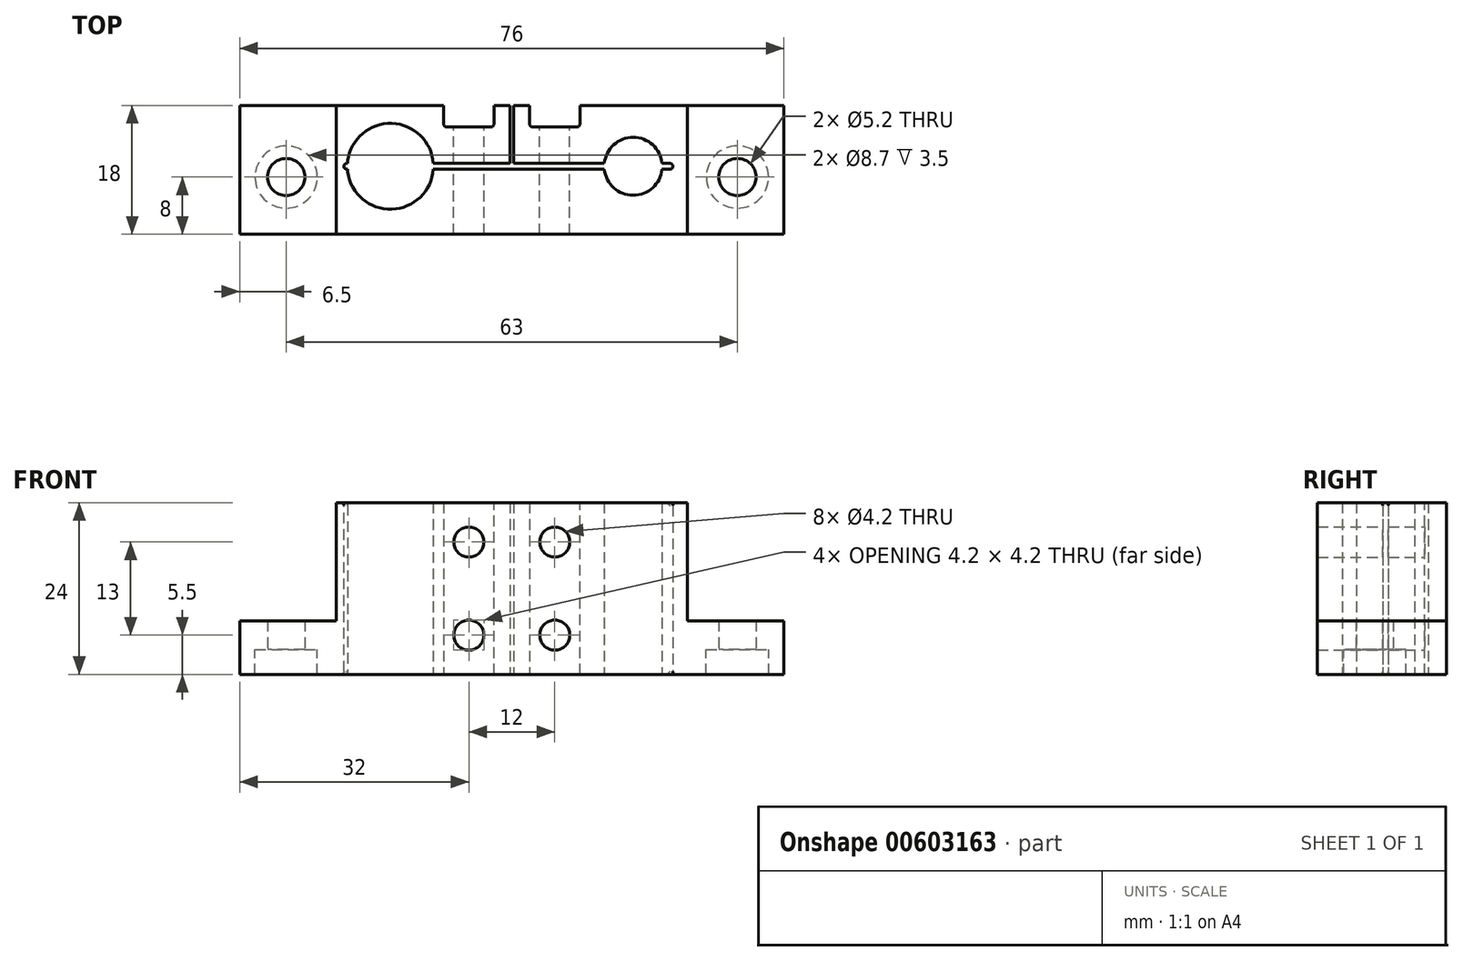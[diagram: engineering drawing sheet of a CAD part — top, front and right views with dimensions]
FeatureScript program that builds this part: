
annotation { "Feature Type Name" : "Feature", "Feature Type Description" : "" }
export const myFeature = defineFeature(function(context is Context, id is Id, definition is map)
    precondition{}
    {
        {
            var Q0;
            Q0=qCreatedBy(makeId("Top.planeOp"),FACE);
            var sketch = newSketch(context, id + "F0", { "sketchPlane" : qUnion([Q0])});
            skLineSegment(sketch, "E0.bottom", {"start": v(-38, 18) * mm, "end": v(38, 18) * mm});
            skLineSegment(sketch, "E0.top", {"start": v(-38, 0) * mm, "end": v(38, 0) * mm});
            skLineSegment(sketch, "E0.left", {"start": v(-38, 18) * mm, "end": v(-38, 0) * mm});
            skLineSegment(sketch, "E0.right", {"start": v(38, 18) * mm, "end": v(38, 0) * mm});
            skLineSegment(sketch, "E1", {"start": v(0, 0) * mm, "end": v(0, 32.17) * mm, "construction": true});
            skCircle(sketch, "E2", {"center": v(-16.95, 9.5) * mm, "radius": 6 * mm});
            skCircle(sketch, "E3", {"center": v(16.95, 9.5) * mm, "radius": 4.05 * mm});
            skCircle(sketch, "E4", {"center": v(31.5, 8) * mm, "radius": 2.6 * mm});
            skCircle(sketch, "E5", {"center": v(-31.5, 8) * mm, "radius": 2.6 * mm});
            skLineSegment(sketch, "E6", {"start": v(-24.5, 18) * mm, "end": v(-24.5, 0) * mm});
            skLineSegment(sketch, "E7", {"start": v(24.5, 18) * mm, "end": v(24.5, 0) * mm});
            skLineSegment(sketch, "E8", {"start": v(12.92, 9.1) * mm, "end": v(-10.96, 9.1) * mm});
            skLineSegment(sketch, "E9", {"start": v(12.92, 9.9) * mm, "end": v(-10.96, 9.9) * mm});
            skLineSegment(sketch, "E10", {"start": v(0.25, 9.9) * mm, "end": v(0.25, 18) * mm});
            skLineSegment(sketch, "E11", {"start": v(-0.25, 9.9) * mm, "end": v(-0.25, 18) * mm});
            skLineSegment(sketch, "E12", {"start": v(-9.5, 0) * mm, "end": v(-9.5, 3) * mm, "construction": true});
            skLineSegment(sketch, "E13", {"start": v(-9.5, 3) * mm, "end": v(-2.5, 3) * mm, "construction": true});
            skLineSegment(sketch, "E14", {"start": v(-2.5, 3) * mm, "end": v(-2.5, 0) * mm, "construction": true});
            skLineSegment(sketch, "E15.MirrorCS", {"start": v(2.5, 3) * mm, "end": v(2.5, 0) * mm, "construction": true});
            skLineSegment(sketch, "E16.MirrorCS", {"start": v(9.5, 3) * mm, "end": v(2.5, 3) * mm, "construction": true});
            skLineSegment(sketch, "E17.MirrorCS", {"start": v(9.5, 0) * mm, "end": v(9.5, 3) * mm, "construction": true});
            skLineSegment(sketch, "E18", {"start": v(-10.96, 9.9) * mm, "end": v(-22.94, 9.9) * mm, "construction": true});
            skLineSegment(sketch, "E19", {"start": v(-22.94, 9.9) * mm, "end": v(-23.45, 9.9) * mm});
            skLineSegment(sketch, "E20", {"start": v(-23.45, 9.9) * mm, "end": v(-23.45, 9.1) * mm});
            skLineSegment(sketch, "E21", {"start": v(-10.96, 9.1) * mm, "end": v(-22.94, 9.1) * mm, "construction": true});
            skLineSegment(sketch, "E22", {"start": v(-22.94, 9.1) * mm, "end": v(-23.45, 9.1) * mm});
            skLineSegment(sketch, "E23.MirrorCS", {"start": v(20.98, 9.1) * mm, "end": v(22.48, 9.1) * mm});
            skLineSegment(sketch, "E24.MirrorCS", {"start": v(20.98, 9.9) * mm, "end": v(22.48, 9.9) * mm});
            skLineSegment(sketch, "E25.MirrorCS", {"start": v(22.48, 9.9) * mm, "end": v(22.48, 9.1) * mm});
            skLineSegment(sketch, "E26", {"start": v(-0.25, 9.9) * mm, "end": v(-0.25, 9.1) * mm});
            skSolve(sketch);
        }
        {
            var Q0;
            {var subQ5=sQuery(id+"F0.wireOp",EDGE,"E6");Q0=makeQuery(id+"F0.imprint","IMPRINT",FACE,{"disambiguationData":[TD([[makeQuery(id+"F0.imprint","IMPRINT",EDGE,{"derivedFrom":subQ5}),1.0]])]});}
            extrude(context, id + "F1", {"entities" : qUnion([Q0]), "depth" : 20.5 * mm, "offsetDistance" : 25 * mm});
        }
        {
            var Q0;
            {var subQ0=sQuery(id+"F0.wireOp",EDGE,"E0.right");Q0=makeQuery(id+"F0.imprint","IMPRINT",FACE,{"disambiguationData":[TD([[makeQuery(id+"F0.imprint","IMPRINT",EDGE,{"derivedFrom":subQ0}),-1.0]])]});}
            var Q1;
            {var subQ0=sQuery(id+"F0.wireOp",EDGE,"E0.left");Q1=makeQuery(id+"F0.imprint","IMPRINT",FACE,{"disambiguationData":[TD([[makeQuery(id+"F0.imprint","IMPRINT",EDGE,{"derivedFrom":subQ0}),1.0]])]});}
            var Q2;
            {var subQ0=sQuery(id+"F0.wireOp",EDGE,"g6wU58Du-NOHn-WXeA-dKv5-i0oWnSDIYxq9");Q2=makeQuery(id+"F0.imprint","IMPRINT",FACE,{"disambiguationData":[TD([[makeQuery(id+"F0.imprint","IMPRINT",EDGE,{"derivedFrom":subQ0}),-1.0]])]});}
            extrude(context, id + "F2", {"entities" : qUnion([Q0, Q1, Q2]), "operationType" : NewBodyOperationType.ADD, "depth" : 4 * mm, "offsetDistance" : 25 * mm});
        }
        {
            var Q0;
            {var subQ0=sQuery(id+"F0.wireOp",EDGE,"E7");var subQ1=sQuery(id+"F0.wireOp",EDGE,"E0.top");var subQ2=sQuery(id+"F0.wireOp",EDGE,"E0.bottom");var subQ3=sQuery(id+"F0.wireOp",EDGE,"E6");Q0=makeQuery(id+"FVCnTTz3T7csswr_4.opBoolean","MERGE",FACE,{"derivedFrom":[makeQuery(id+"F1.opExtrude","CAP_FACE",FACE,{"disambiguationData":[OSD([subQ2,subQ1,sQuery(id+"F0.wireOp",EDGE,"E2"),sQuery(id+"F0.wireOp",EDGE,"E3"),subQ3,subQ0])],"isStart":true}),makeQuery(id+"F2.opExtrude","CAP_FACE",FACE,{"disambiguationData":[OSD([subQ2,subQ1,sQuery(id+"F0.wireOp",EDGE,"E0.left"),sQuery(id+"F0.wireOp",EDGE,"E5"),subQ3])],"isStart":true}),makeQuery(id+"F2.opExtrude","CAP_FACE",FACE,{"disambiguationData":[OSD([subQ2,subQ1,sQuery(id+"F0.wireOp",EDGE,"E0.right"),sQuery(id+"F0.wireOp",EDGE,"E4"),subQ0])],"isStart":true})]});}
            var sketch = newSketch(context, id + "F3", { "sketchPlane" : qUnion([Q0])});
            skCircle(sketch, "E27", {"center": v(-16.95, -9.5) * mm, "radius": 5 * mm});
            skCircle(sketch, "E28", {"center": v(16.95, -9.5) * mm, "radius": 5 * mm});
            skCircle(sketch, "E29", {"center": v(-16.95, -9.5) * mm, "radius": 6 * mm});
            skCircle(sketch, "E30", {"center": v(16.95, -9.5) * mm, "radius": 6 * mm});
            skCircle(sketch, "E31", {"center": v(16.95, -9.5) * mm, "radius": 4.05 * mm});
            skCircle(sketch, "E32", {"center": v(-16.95, -9.5) * mm, "radius": 4 * mm});
            skSolve(sketch);
        }
        {
            var Q0;
            Q0=makeQuery(id+"F3.imprint","IMPRINT",FACE,{"disambiguationData":[TD([[makeQuery(id+"F3.imprint","IMPRINT",EDGE,{"derivedFrom":sQuery(id+"F3.wireOp",EDGE,"E28")}),1.0]])]});
            var Q1;
            Q1=makeQuery(id+"F3.imprint","IMPRINT",FACE,{"disambiguationData":[TD([[makeQuery(id+"F3.imprint","IMPRINT",EDGE,{"derivedFrom":sQuery(id+"F3.wireOp",EDGE,"E27")}),1.0]])]});
            extrude(context, id + "F4", {"entities" : qUnion([Q0, Q1]), "operationType" : NewBodyOperationType.REMOVE, "oppositeDirection" : true, "depth" : 24 * mm, "offsetDistance" : 25 * mm, "hasSecondDirection" : true, "secondDirectionOppositeDirection" : true, "secondDirectionDepth" : 23 * mm});
        }
        {
            var Q0;
            {var subQ0=sQuery(id+"F0.wireOp",EDGE,"E0.bottom");var subQ1=makeQuery(id+"F0.imprint","INTERSECT",VERTEX,{"derivedFrom":[subQ0,sQuery(id+"F0.wireOp",EDGE,"E7")]});Q0=makeQuery(id+"FVCnTTz3T7csswr_4.opBoolean","MERGE",FACE,{"derivedFrom":[makeQuery(id+"F1.opExtrude","SWEPT_FACE",FACE,{"disambiguationData":[OSD([subQ0]),TDD([makeQuery(id+"F0.imprint","IMPRINT",EDGE,{"disambiguationData":[TD([[subQ1,1.0]])],"derivedFrom":subQ0})])]}),makeQuery(id+"F2.opExtrude","SWEPT_FACE",FACE,{"disambiguationData":[OSD([subQ0]),TDD([makeQuery(id+"F0.imprint","IMPRINT",EDGE,{"disambiguationData":[TD([[makeQuery(id+"F0.imprint","INTERSECT",VERTEX,{"derivedFrom":[subQ0,sQuery(id+"F0.wireOp",EDGE,"E0.right")]}),1.0]])],"derivedFrom":subQ0})])]})]});}
            var sketch = newSketch(context, id + "F5", { "sketchPlane" : qUnion([Q0])});
            skLineSegment(sketch, "E33.0.0", {"start": v(-2.5, 0) * mm, "end": v(-9.5, 0) * mm});
            skLineSegment(sketch, "E33.0.1", {"start": v(-9.5, 0) * mm, "end": v(-9.5, 24) * mm});
            skLineSegment(sketch, "E33.0.2", {"start": v(-9.5, 24) * mm, "end": v(-2.5, 24) * mm});
            skLineSegment(sketch, "E33.0.3", {"start": v(-2.5, 24) * mm, "end": v(-2.5, 0) * mm});
            skLineSegment(sketch, "E33.1.0", {"start": v(9.5, 0) * mm, "end": v(2.5, 0) * mm});
            skLineSegment(sketch, "E33.1.1", {"start": v(2.5, 0) * mm, "end": v(2.5, 24) * mm});
            skLineSegment(sketch, "E33.1.2", {"start": v(2.5, 24) * mm, "end": v(9.5, 24) * mm});
            skLineSegment(sketch, "E33.1.3", {"start": v(9.5, 24) * mm, "end": v(9.5, 0) * mm});
            skSolve(sketch);
        }
        {
            var Q0;
            Q0=makeQuery(id+"F5.imprint","IMPRINT",FACE,{"disambiguationData":[TD([[makeQuery(id+"F5.imprint","IMPRINT",EDGE,{"derivedFrom":sQuery(id+"F5.wireOp",EDGE,"E33.0.0")}),-1.0]])]});
            var Q1;
            Q1=makeQuery(id+"F5.imprint","IMPRINT",FACE,{"disambiguationData":[TD([[makeQuery(id+"F5.imprint","IMPRINT",EDGE,{"derivedFrom":sQuery(id+"F5.wireOp",EDGE,"E33.1.0")}),-1.0]])]});
            extrude(context, id + "F6", {"entities" : qUnion([Q0, Q1]), "operationType" : NewBodyOperationType.REMOVE, "oppositeDirection" : true, "depth" : 3 * mm, "offsetDistance" : 25 * mm});
        }
        {
            var Q0;
            {var subQ0=sQuery(id+"F0.wireOp",EDGE,"E7");var subQ1=sQuery(id+"F0.wireOp",EDGE,"E0.top");var subQ2=sQuery(id+"F0.wireOp",EDGE,"E0.bottom");var subQ3=sQuery(id+"F0.wireOp",EDGE,"E6");Q0=makeQuery(id+"FVCnTTz3T7csswr_4.opBoolean","MERGE",FACE,{"derivedFrom":[makeQuery(id+"F1.opExtrude","CAP_FACE",FACE,{"disambiguationData":[OSD([subQ2,subQ1,sQuery(id+"F0.wireOp",EDGE,"E2"),sQuery(id+"F0.wireOp",EDGE,"E3"),subQ3,subQ0,sQuery(id+"F0.wireOp",EDGE,"E8"),sQuery(id+"F0.wireOp",EDGE,"E9"),sQuery(id+"F0.wireOp",EDGE,"E10"),sQuery(id+"F0.wireOp",EDGE,"E11"),sQuery(id+"F0.wireOp",EDGE,"E19"),sQuery(id+"F0.wireOp",EDGE,"E20"),sQuery(id+"F0.wireOp",EDGE,"E22"),sQuery(id+"F0.wireOp",EDGE,"E23.MirrorCS"),sQuery(id+"F0.wireOp",EDGE,"E24.MirrorCS"),sQuery(id+"F0.wireOp",EDGE,"E25.MirrorCS")])],"isStart":true}),makeQuery(id+"F2.opExtrude","CAP_FACE",FACE,{"disambiguationData":[OSD([subQ2,subQ1,sQuery(id+"F0.wireOp",EDGE,"E0.left"),sQuery(id+"F0.wireOp",EDGE,"E5"),subQ3])],"isStart":true}),makeQuery(id+"F2.opExtrude","CAP_FACE",FACE,{"disambiguationData":[OSD([subQ2,subQ1,sQuery(id+"F0.wireOp",EDGE,"E0.right"),sQuery(id+"F0.wireOp",EDGE,"E4"),subQ0])],"isStart":true})]});}
            var sketch = newSketch(context, id + "F7", { "sketchPlane" : qUnion([Q0])});
            skCircle(sketch, "E34", {"center": v(31.5, -8) * mm, "radius": 4.35 * mm});
            skCircle(sketch, "E35", {"center": v(-31.5, -8) * mm, "radius": 4.35 * mm});
            skSolve(sketch);
        }
        {
            var Q0;
            Q0=makeQuery(id+"F7.imprint","IMPRINT",FACE,{"disambiguationData":[TD([[makeQuery(id+"F7.imprint","IMPRINT",EDGE,{"derivedFrom":sQuery(id+"F7.wireOp",EDGE,"E34")}),-1.0]])]});
            extrude(context, id + "F8", {"entities" : qUnion([Q0]), "operationType" : NewBodyOperationType.ADD, "depth" : 3.5 * mm, "offsetDistance" : 25 * mm});
        }
        {
            var Q0;
            {var subQ0=sQuery(id+"F0.wireOp",EDGE,"E20");Q0=makeQuery(id+"F8.boolean.opBoolean","MERGE",FACE,{"derivedFrom":[makeQuery(id+"F1.opExtrude","SWEPT_FACE",FACE,{"disambiguationData":[OSD([subQ0])]}),makeQuery(id+"F8.opExtrude","SWEPT_FACE",FACE,{"disambiguationData":[OSD([subQ0])]})]});}
            var Q1;
            {var subQ0=sQuery(id+"F0.wireOp",EDGE,"E25.MirrorCS");Q1=makeQuery(id+"F8.boolean.opBoolean","MERGE",FACE,{"derivedFrom":[makeQuery(id+"F1.opExtrude","SWEPT_FACE",FACE,{"disambiguationData":[OSD([subQ0])]}),makeQuery(id+"F8.opExtrude","SWEPT_FACE",FACE,{"disambiguationData":[OSD([subQ0])]})]});}
            var Q2;
            Q2=makeQuery(id+"F2.opExtrude","CAP_EDGE",EDGE,{"disambiguationData":[OSD([sQuery(id+"F0.wireOp",EDGE,"E7")])],"isStart":false});
            var Q3;
            Q3=makeQuery(id+"F2.opExtrude","CAP_EDGE",EDGE,{"disambiguationData":[OSD([sQuery(id+"F0.wireOp",EDGE,"E6")])],"isStart":false});
            var Q4;
            {var subQ0=sQuery(id+"F5.wireOp",EDGE,"E33.0.0");var subQ1=sQuery(id+"F5.wireOp",EDGE,"E33.0.1");var subQ2=sQuery(id+"F0.wireOp",EDGE,"E0.bottom");Q4=makeQuery(id+"F8.boolean.opBoolean","MERGE",EDGE,{"derivedFrom":[makeQuery(id+"F6.boolean.opBoolean","COPY",EDGE,{"derivedFrom":makeQuery(id+"F6.opExtrude","CAP_EDGE",EDGE,{"disambiguationData":[OSD([subQ1])],"isStart":false})}),makeQuery(id+"F8.opExtrude","SWEPT_EDGE",EDGE,{"disambiguationData":[OSD([subQ2,subQ0,subQ1]),TDD([makeQuery(id+"F7.imprint","INTERSECT",VERTEX,{"derivedFrom":[makeQuery(id+"F6.boolean.opBoolean","COPY",EDGE,{"derivedFrom":makeQuery(id+"F6.opExtrude","SWEPT_EDGE",EDGE,{"disambiguationData":[OSD([subQ2,subQ0,subQ1])]})}),makeQuery(id+"F6.boolean.opBoolean","COPY",EDGE,{"derivedFrom":makeQuery(id+"F6.opExtrude","CAP_EDGE",EDGE,{"disambiguationData":[OSD([subQ0])],"isStart":false})})]})])]})]});}
            var Q5;
            {var subQ0=sQuery(id+"F5.wireOp",EDGE,"E33.0.0");var subQ1=sQuery(id+"F5.wireOp",EDGE,"E33.0.3");var subQ2=sQuery(id+"F0.wireOp",EDGE,"E0.bottom");Q5=makeQuery(id+"F8.boolean.opBoolean","MERGE",EDGE,{"derivedFrom":[makeQuery(id+"F6.boolean.opBoolean","COPY",EDGE,{"derivedFrom":makeQuery(id+"F6.opExtrude","CAP_EDGE",EDGE,{"disambiguationData":[OSD([subQ1])],"isStart":false})}),makeQuery(id+"F8.opExtrude","SWEPT_EDGE",EDGE,{"disambiguationData":[OSD([subQ2,subQ0,subQ1]),TDD([makeQuery(id+"F7.imprint","INTERSECT",VERTEX,{"derivedFrom":[makeQuery(id+"F6.boolean.opBoolean","COPY",EDGE,{"derivedFrom":makeQuery(id+"F6.opExtrude","SWEPT_EDGE",EDGE,{"disambiguationData":[OSD([subQ2,subQ0,subQ1])]})}),makeQuery(id+"F6.boolean.opBoolean","COPY",EDGE,{"derivedFrom":makeQuery(id+"F6.opExtrude","CAP_EDGE",EDGE,{"disambiguationData":[OSD([subQ0])],"isStart":false})})]})])]})]});}
            var Q6;
            {var subQ0=sQuery(id+"F5.wireOp",EDGE,"E33.1.3");Q6=makeQuery(id+"F8.boolean.opBoolean","MERGE",EDGE,{"derivedFrom":[makeQuery(id+"F6.boolean.opBoolean","COPY",EDGE,{"derivedFrom":makeQuery(id+"F6.opExtrude","CAP_EDGE",EDGE,{"disambiguationData":[OSD([subQ0])],"isStart":false})}),makeQuery(id+"F8.opExtrude","SWEPT_EDGE",EDGE,{"disambiguationData":[OSD([sQuery(id+"F5.wireOp",EDGE,"E33.1.0"),subQ0])]})]});}
            var Q7;
            {var subQ0=sQuery(id+"F5.wireOp",EDGE,"E33.1.1");Q7=makeQuery(id+"F8.boolean.opBoolean","MERGE",EDGE,{"derivedFrom":[makeQuery(id+"F6.boolean.opBoolean","COPY",EDGE,{"derivedFrom":makeQuery(id+"F6.opExtrude","CAP_EDGE",EDGE,{"disambiguationData":[OSD([subQ0])],"isStart":false})}),makeQuery(id+"F8.opExtrude","SWEPT_EDGE",EDGE,{"disambiguationData":[OSD([sQuery(id+"F5.wireOp",EDGE,"E33.1.0"),subQ0])]})]});}
            var Q8;
            Q8=makeQuery(id+"F8.opExtrude","CAP_EDGE",EDGE,{"disambiguationData":[OSD([sQuery(id+"F7.wireOp",EDGE,"E35")])],"isStart":true});
            var Q9;
            Q9=makeQuery(id+"F8.opExtrude","CAP_EDGE",EDGE,{"disambiguationData":[OSD([sQuery(id+"F7.wireOp",EDGE,"E34")])],"isStart":true});
            fillet(context, id + "F9", {"entities" : qUnion([Q0, Q1, Q2, Q3, Q4, Q5, Q6, Q7, Q8, Q9]), "radius" : .4 * mm, "allowEdgeOverflow" : false});
        }
        {
            var Q0;
            Q0=qCreatedBy(makeId("Front.planeOp"),FACE);
            var sketch = newSketch(context, id + "F10", { "sketchPlane" : qUnion([Q0])});
            skPoint(sketch, "E36", {"position": v(-6, 2) * mm});
            skPoint(sketch, "E37.0.1.0", {"position": v(-6, 15) * mm});
            skPoint(sketch, "E37.1.0.0", {"position": v(6, 2) * mm});
            skPoint(sketch, "E37.1.1.0", {"position": v(6, 15) * mm});
            skLineSegment(sketch, "E37.direction1", {"start": v(-6, 2) * mm, "end": v(6, 2) * mm, "construction": true});
            skLineSegment(sketch, "E37.direction2", {"start": v(-6, 2) * mm, "end": v(-6, 15) * mm, "construction": true});
            skSolve(sketch);
        }
        {
            var Q0;
            Q0=sQuery(id+"F10.wireOp",VERTEX,"E37.1.0.0");
            var Q1;
            Q1=sQuery(id+"F10.wireOp",VERTEX,"E36");
            var Q2;
            Q2=sQuery(id+"F10.wireOp",VERTEX,"E37.0.1.0");
            var Q3;
            Q3=sQuery(id+"F10.wireOp",VERTEX,"E37.1.1.0");
            var Q4;
            Q4=makeQuery(id+"F1.opExtrude","SWEPT_BODY",BODY,{"disambiguationData":[OSD([sQuery(id+"F0.wireOp",EDGE,"E0.bottom"),sQuery(id+"F0.wireOp",EDGE,"E0.top"),sQuery(id+"F0.wireOp",EDGE,"E2"),sQuery(id+"F0.wireOp",EDGE,"E3"),sQuery(id+"F0.wireOp",EDGE,"E6"),sQuery(id+"F0.wireOp",EDGE,"E7"),sQuery(id+"F0.wireOp",EDGE,"E8"),sQuery(id+"F0.wireOp",EDGE,"E9"),sQuery(id+"F0.wireOp",EDGE,"E10"),sQuery(id+"F0.wireOp",EDGE,"E11")])]});
            hole(context, id + "F11", {"style" : HoleStyle.SIMPLE, "endStyle" : HoleEndStyle.THROUGH, "holeDiameter" : 4.2 * mm, "majorDiameter" : 5 * mm, "isTappedThrough" : true, "tappedDepth" : 6 * mm, "tapClearance" : 3, "startFromSketch" : true, "locations" : qUnion([Q0, Q1, Q2, Q3]), "scope" : qUnion([Q4])});
        }
    });
